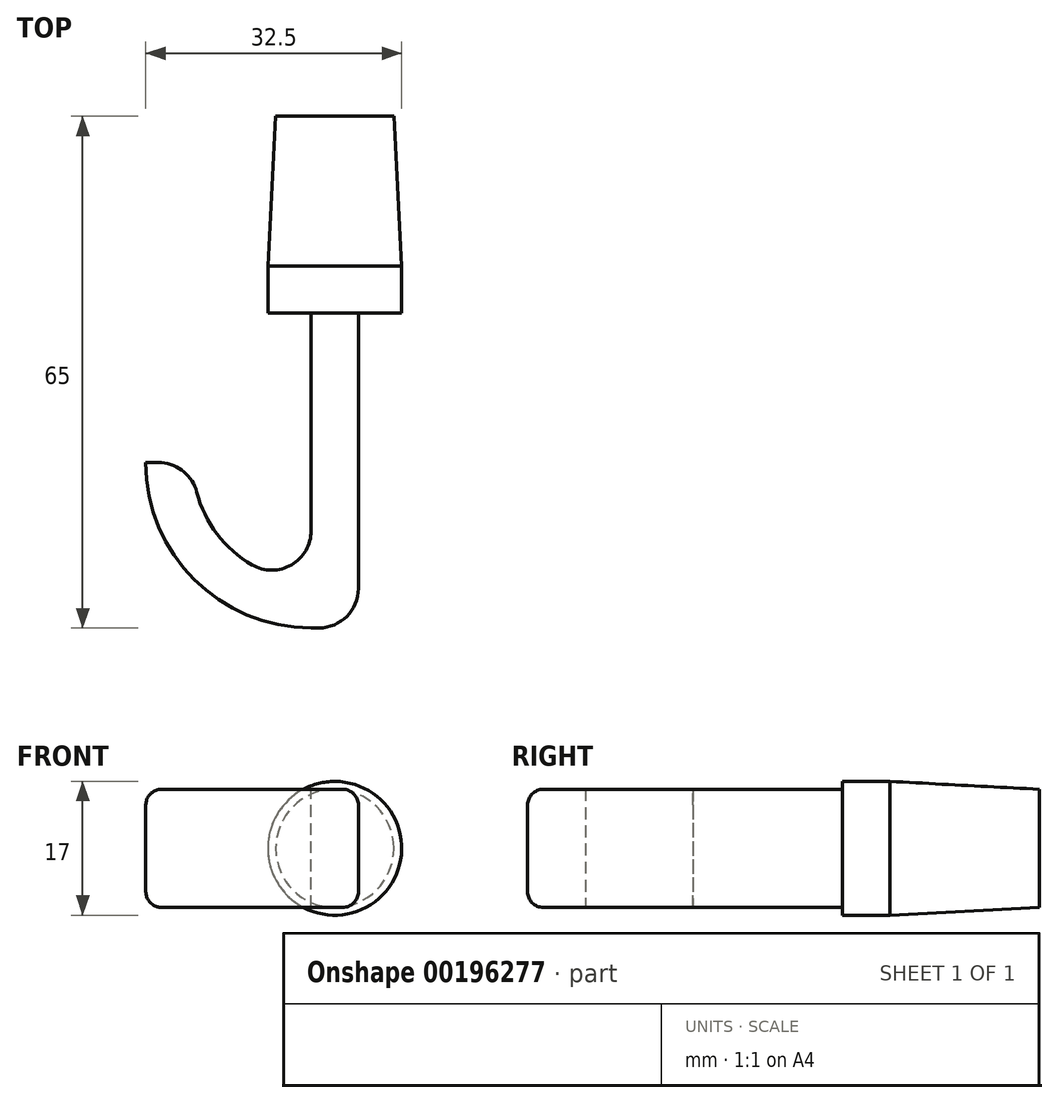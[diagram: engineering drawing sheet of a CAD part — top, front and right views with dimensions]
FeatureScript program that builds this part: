
annotation { "Feature Type Name" : "Feature", "Feature Type Description" : "" }
export const myFeature = defineFeature(function(context is Context, id is Id, definition is map)
    precondition{}
    {
        {
            var Q0;
            Q0=qCreatedBy(makeId("Top.planeOp"),FACE);
            var sketch = newSketch(context, id + "F0", { "sketchPlane" : qUnion([Q0])});
            skArc(sketch, "E0", {"start": v(0, -21) * mm, "mid": v(-14.85, -14.85) * mm, "end": v(-21, 0) * mm});
            skLineSegment(sketch, "E1", {"start": v(0, 0) * mm, "end": v(0, -15) * mm, "construction": true});
            skArc(sketch, "E2", {"start": v(0, -15) * mm, "mid": v(-10.6, -10.6) * mm, "end": v(-15, 0) * mm});
            skLineSegment(sketch, "E3", {"start": v(-21, 0) * mm, "end": v(-15, 0) * mm});
            skLineSegment(sketch, "E4", {"start": v(0, 0) * mm, "end": v(0, -21) * mm});
            skLineSegment(sketch, "E5.bottom", {"start": v(0, -21) * mm, "end": v(6, -21) * mm});
            skLineSegment(sketch, "E5.top", {"start": v(0, 19) * mm, "end": v(6, 19) * mm});
            skLineSegment(sketch, "E5.left", {"start": v(0, -21) * mm, "end": v(0, 19) * mm});
            skLineSegment(sketch, "E5.right", {"start": v(6, -21) * mm, "end": v(6, 19) * mm});
            skSolve(sketch);
        }
        {
            var Q0;
            Q0 = qSketchRegion(id + "F0", true);
            extrude(context, id + "F1", {"entities" : qUnion([Q0]), "depth" : 15 * mm});
        }
        {
            var Q0;
            Q0=makeQuery(id+"F1.opExtrude","SWEPT_FACE",FACE,{"disambiguationData":[OSD([sQuery(id+"F0.wireOp",EDGE,"E5.top")])]});
            var sketch = newSketch(context, id + "F2", { "sketchPlane" : qUnion([Q0])});
            skLineSegment(sketch, "E6", {"start": v(-6, 15) * mm, "end": v(0, 0) * mm, "construction": true});
            skLineSegment(sketch, "E7", {"start": v(0, 0) * mm, "end": v(-6, 0) * mm, "construction": true});
            skLineSegment(sketch, "E8", {"start": v(-6, 0) * mm, "end": v(0, 15) * mm, "construction": true});
            skCircle(sketch, "E9", {"center": v(-3, 7.5) * mm, "radius": 8.5 * mm});
            skSolve(sketch);
        }
        {
            var Q0;
            Q0=makeQuery(id+"F2.imprint","IMPRINT",FACE,{"disambiguationData":[TD([[makeQuery(id+"F2.imprint","IMPRINT",EDGE,{"derivedFrom":sQuery(id+"F2.wireOp",EDGE,"E9")}),1.0]])]});
            var Q1;
            {var subQ0=sQuery(id+"F0.wireOp",EDGE,"E5.top");Q1=makeQuery(id+"F2.imprint","IMPRINT",FACE,{"disambiguationData":[TD([[makeQuery(id+"F2.imprint","IMPRINT",EDGE,{"derivedFrom":makeQuery(id+"F1.opExtrude","CAP_EDGE",EDGE,{"disambiguationData":[OSD([subQ0])],"isStart":true})}),-1.0]])]});}
            extrude(context, id + "F3", {"entities" : qUnion([Q0, Q1]), "operationType" : NewBodyOperationType.ADD, "depth" : 25 * mm});
        }
        {
            var Q0;
            Q0=makeQuery(id+"F3.opExtrude","CAP_EDGE",EDGE,{"disambiguationData":[OSD([sQuery(id+"F2.wireOp",EDGE,"E9")])],"isStart":false});
            chamfer(context, id + "F4", {"entities" : qUnion([Q0]), "chamferType" : ChamferType.TWO_OFFSETS, "width1" : 1 * mm, "oppositeDirection" : false, "width2" : 19 * mm, "tangentPropagation" : true});
        }
        {
            var Q0;
            Q0=makeQuery(id+"F1.opExtrude","CAP_EDGE",EDGE,{"disambiguationData":[OSD([sQuery(id+"F0.wireOp",EDGE,"E5.right")])],"isStart":false});
            var Q1;
            Q1=makeQuery(id+"F1.opExtrude","CAP_EDGE",EDGE,{"disambiguationData":[OSD([sQuery(id+"F0.wireOp",EDGE,"E0")])],"isStart":false});
            var Q2;
            Q2=makeQuery(id+"F1.opExtrude","CAP_EDGE",EDGE,{"disambiguationData":[OSD([sQuery(id+"F0.wireOp",EDGE,"E5.bottom")])],"isStart":true});
            var Q3;
            Q3=makeQuery(id+"F1.opExtrude","CAP_EDGE",EDGE,{"disambiguationData":[OSD([sQuery(id+"F0.wireOp",EDGE,"E0")])],"isStart":true});
            var Q4;
            Q4=makeQuery(id+"F1.opExtrude","CAP_EDGE",EDGE,{"disambiguationData":[OSD([sQuery(id+"F0.wireOp",EDGE,"E5.right")])],"isStart":true});
            fillet(context, id + "F5", {"entities" : qUnion([Q0, Q1, Q2, Q3, Q4]), "radius" : 2 * mm, "tangentPropagation" : true, "allowEdgeOverflow" : false});
        }
        {
            var Q0;
            Q0=makeQuery(id+"F1.opExtrude","SWEPT_EDGE",EDGE,{"disambiguationData":[OSD([sQuery(id+"F0.wireOp",EDGE,"E2"),sQuery(id+"F0.wireOp",EDGE,"E5.left")])]});
            fillet(context, id + "F6", {"entities" : qUnion([Q0]), "radius" : 5 * mm, "tangentPropagation" : true, "allowEdgeOverflow" : false});
        }
        {
            var Q0;
            Q0=makeQuery(id+"F1.opExtrude","SWEPT_EDGE",EDGE,{"disambiguationData":[OSD([sQuery(id+"F0.wireOp",EDGE,"E5.bottom"),sQuery(id+"F0.wireOp",EDGE,"E5.right")])]});
            fillet(context, id + "F7", {"entities" : qUnion([Q0]), "radius" : 5 * mm, "tangentPropagation" : true, "allowEdgeOverflow" : false});
        }
    });
